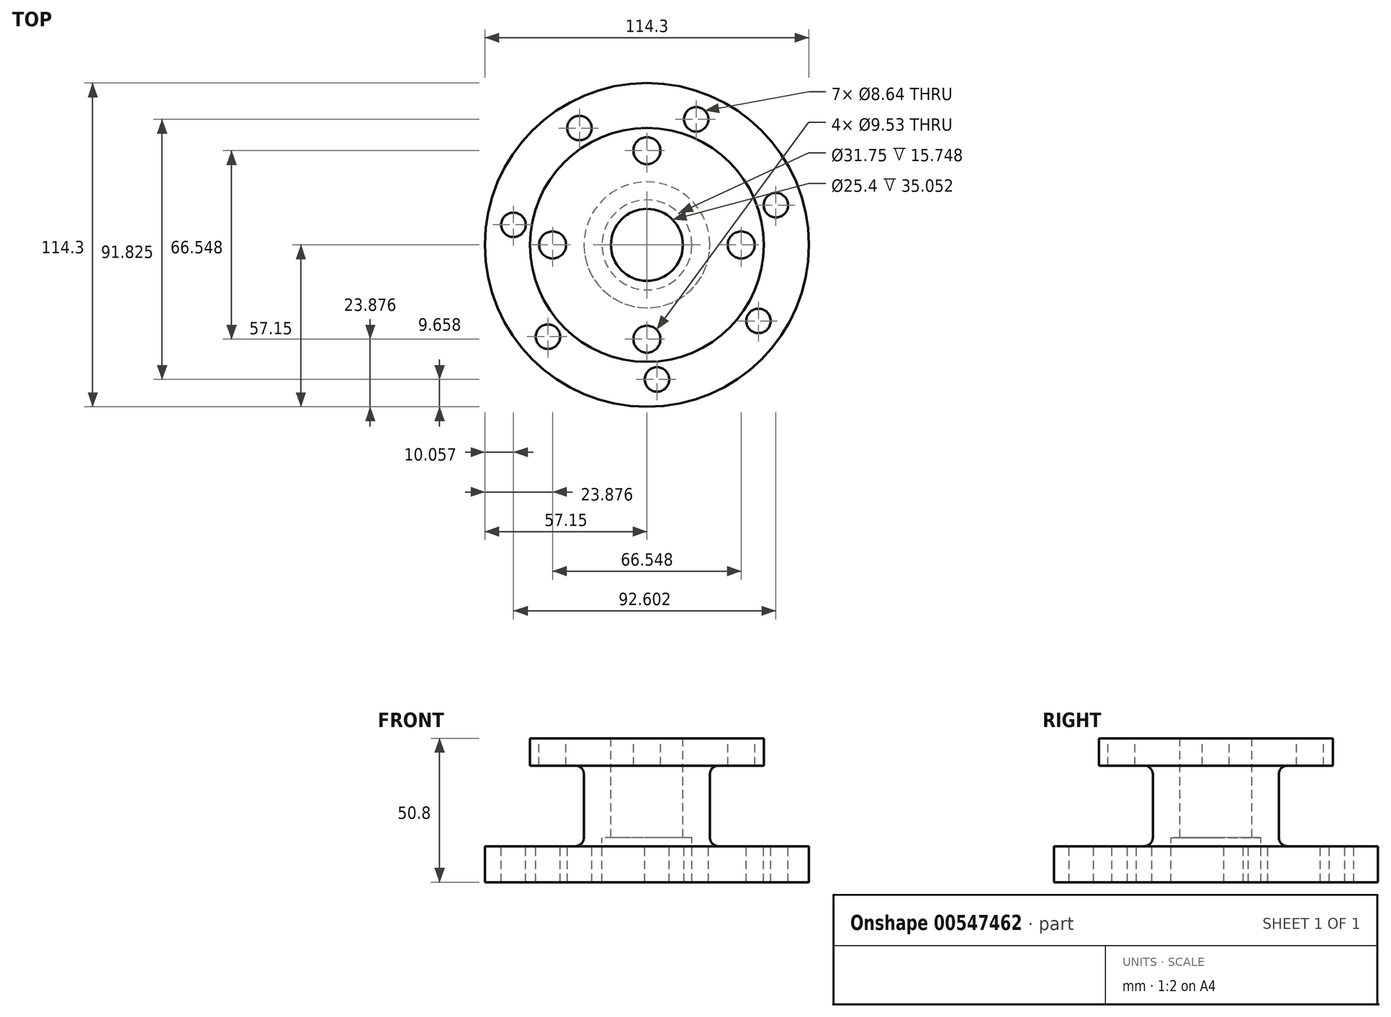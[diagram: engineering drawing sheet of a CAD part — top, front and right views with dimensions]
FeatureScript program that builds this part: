
annotation { "Feature Type Name" : "Feature", "Feature Type Description" : "" }
export const myFeature = defineFeature(function(context is Context, id is Id, definition is map)
    precondition{}
    {
        {
            var Q0;
            Q0=qCreatedBy(makeId("Front.planeOp"),FACE);
            var sketch = newSketch(context, id + "F0", { "sketchPlane" : qUnion([Q0])});
            skLineSegment(sketch, "E0", {"start": v(0, 75.5) * mm, "end": v(0, -73.24) * mm, "construction": true});
            skLineSegment(sketch, "E1", {"start": v(-57.15, -15.75) * mm, "end": v(-57.15, -3.05) * mm});
            skLineSegment(sketch, "E2", {"start": v(-57.15, -3.05) * mm, "end": v(-22.22, -3.05) * mm});
            skLineSegment(sketch, "E3", {"start": v(-22.22, -3.05) * mm, "end": v(-22.23, 25.4) * mm});
            skLineSegment(sketch, "E4", {"start": v(-22.23, 25.4) * mm, "end": v(-41.28, 25.4) * mm});
            skLineSegment(sketch, "E5", {"start": v(-41.28, 25.4) * mm, "end": v(-41.28, 35.05) * mm});
            skLineSegment(sketch, "E6", {"start": v(-41.28, 35.05) * mm, "end": v(-12.7, 35.05) * mm});
            skLineSegment(sketch, "E7", {"start": v(-12.7, 35.05) * mm, "end": v(-12.7, 0) * mm});
            skLineSegment(sketch, "E8", {"start": v(-12.7, 0) * mm, "end": v(-15.87, 0) * mm});
            skLineSegment(sketch, "E9", {"start": v(-15.87, 0) * mm, "end": v(-15.87, -15.75) * mm});
            skLineSegment(sketch, "E10", {"start": v(-15.88, -15.75) * mm, "end": v(-57.15, -15.75) * mm});
            skSolve(sketch);
        }
        {
            var Q0;
            Q0=makeQuery(id+"F0.imprint","IMPRINT",FACE,{"disambiguationData":[TD([[makeQuery(id+"F0.imprint","IMPRINT",EDGE,{"derivedFrom":sQuery(id+"F0.wireOp",EDGE,"E1")}),-1.0]])]});
            var Q1;
            Q1=sQuery(id+"F0.wireOp",EDGE,"E0");
            revolve(context, id + "F1", {"entities" : qUnion([Q0]), "axis" : qUnion([Q1]), "revolveType" : RevolveType.FULL});
        }
        {
            var Q0;
            Q0=makeQuery(id+"F1.opRevolve","SWEPT_FACE",FACE,{"disambiguationData":[OSD([sQuery(id+"F0.wireOp",EDGE,"E6")])]});
            var sketch = newSketch(context, id + "F2", { "sketchPlane" : qUnion([Q0])});
            skCircle(sketch, "E11", {"center": v(0, 0) * mm, "radius": 33.27 * mm});
            skLineSegment(sketch, "E12", {"start": v(0, 0) * mm, "end": v(0, 78.68) * mm, "construction": true});
            skLineSegment(sketch, "E13", {"start": v(0, 78.68) * mm, "end": v(0, 0) * mm, "construction": true});
            skLineSegment(sketch, "E14", {"start": v(0, 0) * mm, "end": v(-69.23, 39.97) * mm, "construction": true});
            skCircle(sketch, "E15", {"center": v(0, 33.27) * mm, "radius": 4.76 * mm});
            skCircle(sketch, "E16.1.0", {"center": v(-33.27, 0) * mm, "radius": 4.76 * mm});
            skCircle(sketch, "E16.2.0", {"center": v(0, -33.27) * mm, "radius": 4.76 * mm});
            skCircle(sketch, "E16.3.0", {"center": v(33.27, 0) * mm, "radius": 4.76 * mm});
            skSolve(sketch);
        }
        {
            var Q0;
            Q0=makeQuery(id+"F1.opRevolve","SWEPT_FACE",FACE,{"disambiguationData":[OSD([sQuery(id+"F0.wireOp",EDGE,"E2")])]});
            var sketch = newSketch(context, id + "F3", { "sketchPlane" : qUnion([Q0])});
            skSolve(sketch);
        }
        {
            var Q0;
            {var subQ0=sQuery(id+"F2.wireOp",EDGE,"E15");var subQ1=sQuery(id+"F2.wireOp",EDGE,"E11");var subQ2=makeQuery(id+"F2.imprint","INTERSECT",VERTEX,{"disambiguationData":[OD(0.0)],"derivedFrom":[subQ1,subQ0]});Q0=makeQuery(id+"F2.imprint","IMPRINT",FACE,{"disambiguationData":[TD([[makeQuery(id+"F2.imprint","IMPRINT",EDGE,{"disambiguationData":[TD([[subQ2,-1.0]])],"derivedFrom":subQ1}),1.0]])]});}
            var Q1;
            {var subQ0=sQuery(id+"F2.wireOp",EDGE,"E15");var subQ1=sQuery(id+"F2.wireOp",EDGE,"E11");var subQ2=makeQuery(id+"F2.imprint","INTERSECT",VERTEX,{"disambiguationData":[OD(0.0)],"derivedFrom":[subQ1,subQ0]});Q1=makeQuery(id+"F2.imprint","IMPRINT",FACE,{"disambiguationData":[TD([[makeQuery(id+"F2.imprint","IMPRINT",EDGE,{"disambiguationData":[TD([[subQ2,-1.0]])],"derivedFrom":subQ1}),-1.0]])]});}
            var Q2;
            {var subQ0=sQuery(id+"F2.wireOp",EDGE,"E16.3.0");var subQ1=sQuery(id+"F2.wireOp",EDGE,"E11");var subQ2=makeQuery(id+"F2.imprint","INTERSECT",VERTEX,{"disambiguationData":[OD(0.0)],"derivedFrom":[subQ1,subQ0]});Q2=makeQuery(id+"F2.imprint","IMPRINT",FACE,{"disambiguationData":[TD([[makeQuery(id+"F2.imprint","IMPRINT",EDGE,{"disambiguationData":[TD([[subQ2,1.0]])],"derivedFrom":subQ1}),1.0]])]});}
            var Q3;
            {var subQ0=sQuery(id+"F2.wireOp",EDGE,"E16.3.0");var subQ1=sQuery(id+"F2.wireOp",EDGE,"E11");var subQ2=makeQuery(id+"F2.imprint","INTERSECT",VERTEX,{"disambiguationData":[OD(0.0)],"derivedFrom":[subQ1,subQ0]});Q3=makeQuery(id+"F2.imprint","IMPRINT",FACE,{"disambiguationData":[TD([[makeQuery(id+"F2.imprint","IMPRINT",EDGE,{"disambiguationData":[TD([[subQ2,1.0]])],"derivedFrom":subQ1}),-1.0]])]});}
            var Q4;
            {var subQ0=sQuery(id+"F2.wireOp",EDGE,"E16.2.0");var subQ1=sQuery(id+"F2.wireOp",EDGE,"E11");var subQ2=makeQuery(id+"F2.imprint","INTERSECT",VERTEX,{"disambiguationData":[OD(0.0)],"derivedFrom":[subQ1,subQ0]});Q4=makeQuery(id+"F2.imprint","IMPRINT",FACE,{"disambiguationData":[TD([[makeQuery(id+"F2.imprint","IMPRINT",EDGE,{"disambiguationData":[TD([[subQ2,-1.0]])],"derivedFrom":subQ1}),-1.0]])]});}
            var Q5;
            {var subQ0=sQuery(id+"F2.wireOp",EDGE,"E16.2.0");var subQ1=sQuery(id+"F2.wireOp",EDGE,"E11");var subQ2=makeQuery(id+"F2.imprint","INTERSECT",VERTEX,{"disambiguationData":[OD(0.0)],"derivedFrom":[subQ1,subQ0]});Q5=makeQuery(id+"F2.imprint","IMPRINT",FACE,{"disambiguationData":[TD([[makeQuery(id+"F2.imprint","IMPRINT",EDGE,{"disambiguationData":[TD([[subQ2,-1.0]])],"derivedFrom":subQ1}),1.0]])]});}
            var Q6;
            {var subQ0=sQuery(id+"F2.wireOp",EDGE,"E16.1.0");var subQ1=sQuery(id+"F2.wireOp",EDGE,"E11");var subQ2=makeQuery(id+"F2.imprint","INTERSECT",VERTEX,{"disambiguationData":[OD(0.0)],"derivedFrom":[subQ1,subQ0]});Q6=makeQuery(id+"F2.imprint","IMPRINT",FACE,{"disambiguationData":[TD([[makeQuery(id+"F2.imprint","IMPRINT",EDGE,{"disambiguationData":[TD([[subQ2,-1.0]])],"derivedFrom":subQ1}),1.0]])]});}
            var Q7;
            {var subQ0=sQuery(id+"F2.wireOp",EDGE,"E16.1.0");var subQ1=sQuery(id+"F2.wireOp",EDGE,"E11");var subQ2=makeQuery(id+"F2.imprint","INTERSECT",VERTEX,{"disambiguationData":[OD(0.0)],"derivedFrom":[subQ1,subQ0]});Q7=makeQuery(id+"F2.imprint","IMPRINT",FACE,{"disambiguationData":[TD([[makeQuery(id+"F2.imprint","IMPRINT",EDGE,{"disambiguationData":[TD([[subQ2,-1.0]])],"derivedFrom":subQ1}),-1.0]])]});}
            extrude(context, id + "F4", {"entities" : qUnion([Q0, Q1, Q2, Q3, Q4, Q5, Q6, Q7]), "operationType" : NewBodyOperationType.REMOVE, "endBound" : BoundingType.UP_TO_NEXT, "oppositeDirection" : true, "depth" : 25.4 * mm, "offsetDistance" : 25.4 * mm});
        }
        {
            var Q0;
            {var subQ0=sQuery(id+"F0.wireOp",EDGE,"E2");Q0=makeQuery(id+"F3.imprint","IMPRINT",FACE,{"disambiguationData":[TD([[makeQuery(id+"F3.imprint","IMPRINT",EDGE,{"derivedFrom":makeQuery(id+"F1.opRevolve","SWEPT_EDGE",EDGE,{"disambiguationData":[OSD([sQuery(id+"F0.wireOp",EDGE,"E1"),subQ0])]})}),1.0]])]});}
            var sketch = newSketch(context, id + "F5", { "sketchPlane" : qUnion([Q0])});
            skCircle(sketch, "E17", {"center": v(0, 0) * mm, "radius": 47.63 * mm, "construction": true});
            skLineSegment(sketch, "E18", {"start": v(0, 0) * mm, "end": v(-36.53, 63.28) * mm, "construction": true});
            skLineSegment(sketch, "E19", {"start": v(0, 0) * mm, "end": v(-86.02, 0) * mm, "construction": true});
            skCircle(sketch, "E20", {"center": v(-23.81, 41.24) * mm, "radius": 4.32 * mm});
            skCircle(sketch, "E21.1.0", {"center": v(-47.1, 7.1) * mm, "radius": 4.32 * mm});
            skCircle(sketch, "E21.2.0", {"center": v(-34.91, -32.4) * mm, "radius": 4.32 * mm});
            skCircle(sketch, "E21.3.0", {"center": v(3.56, -47.5) * mm, "radius": 4.32 * mm});
            skCircle(sketch, "E21.4.0", {"center": v(39.35, -26.83) * mm, "radius": 4.32 * mm});
            skCircle(sketch, "E21.5.0", {"center": v(45.5, 14.04) * mm, "radius": 4.32 * mm});
            skCircle(sketch, "E21.6.0", {"center": v(17.4, 44.33) * mm, "radius": 4.32 * mm});
            skSolve(sketch);
        }
        {
            var Q0;
            Q0 = qSketchRegion(id + "F5", true);
            extrude(context, id + "F6", {"entities" : qUnion([Q0]), "operationType" : NewBodyOperationType.REMOVE, "endBound" : BoundingType.UP_TO_NEXT, "oppositeDirection" : true, "depth" : 25.4 * mm, "offsetDistance" : 25.4 * mm});
        }
        {
            var Q0;
            Q0=makeQuery(id+"F1.opRevolve","SWEPT_EDGE",EDGE,{"disambiguationData":[OSD([sQuery(id+"F0.wireOp",EDGE,"E2"),sQuery(id+"F0.wireOp",EDGE,"E3")])]});
            var Q1;
            Q1=makeQuery(id+"F1.opRevolve","SWEPT_EDGE",EDGE,{"disambiguationData":[OSD([sQuery(id+"F0.wireOp",EDGE,"E3"),sQuery(id+"F0.wireOp",EDGE,"E4")])]});
            fillet(context, id + "F7", {"entities" : qUnion([Q0, Q1]), "radius" : 3.05 * mm, "tangentPropagation" : true, "allowEdgeOverflow" : false});
        }
    });
